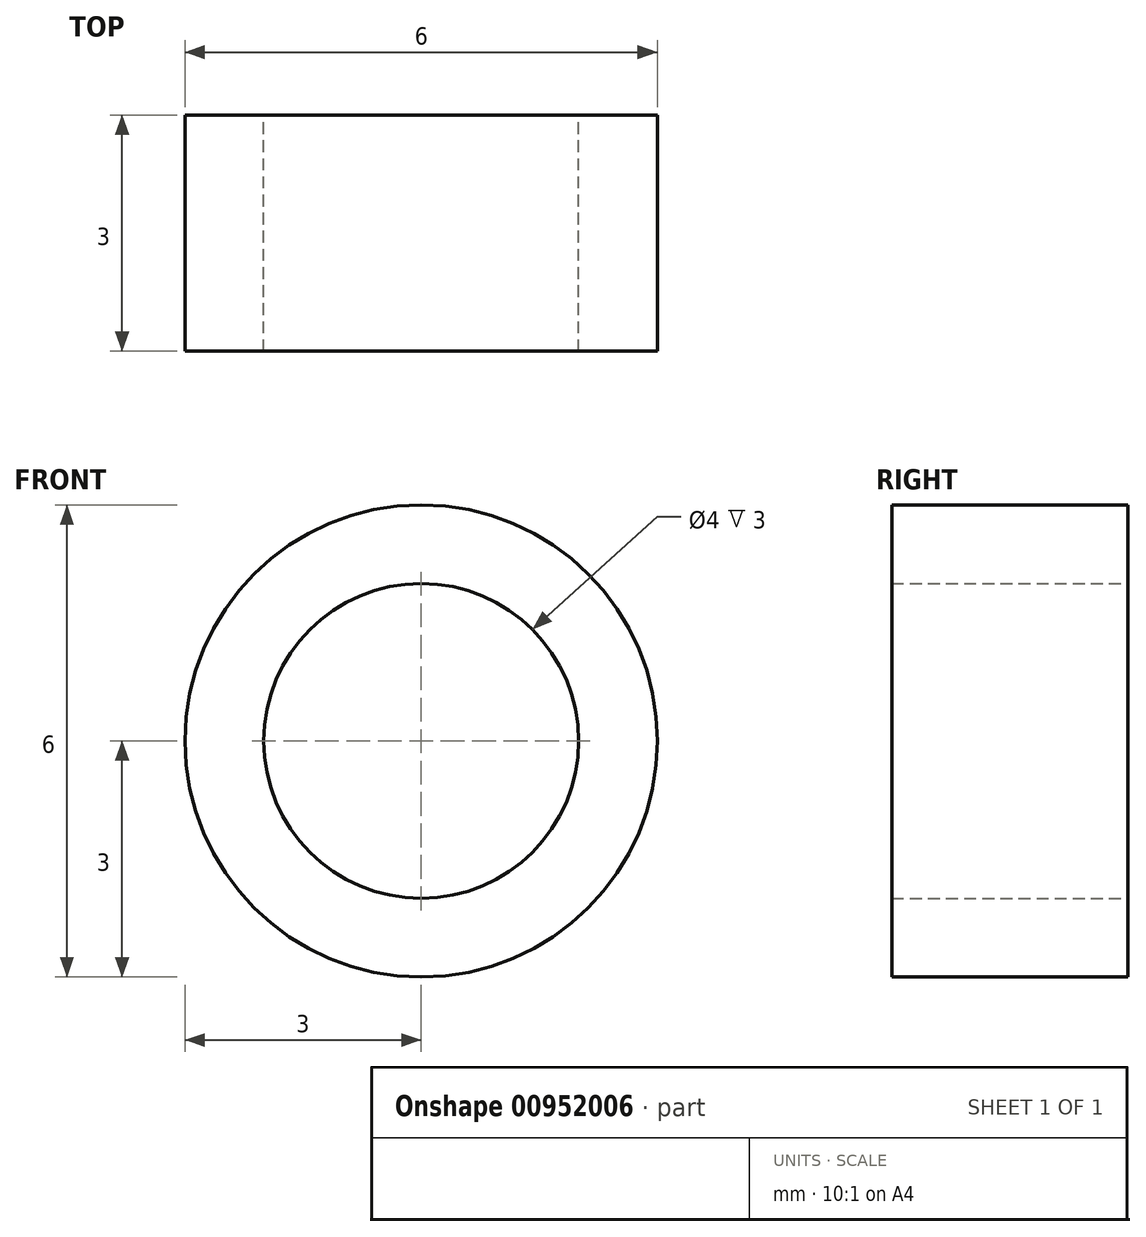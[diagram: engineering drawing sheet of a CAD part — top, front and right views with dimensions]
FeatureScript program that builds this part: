
annotation { "Feature Type Name" : "Feature", "Feature Type Description" : "" }
export const myFeature = defineFeature(function(context is Context, id is Id, definition is map)
    precondition{}
    {
        {
            var Q0;
            Q0=qCreatedBy(makeId("Front.planeOp"),FACE);
            var sketch = newSketch(context, id + "F0", { "sketchPlane" : qUnion([Q0])});
            skCircle(sketch, "E0", {"center": v(0, 0) * mm, "radius": 3 * mm});
            skCircle(sketch, "E1", {"center": v(0, 0) * mm, "radius": 2 * mm});
            skSolve(sketch);
        }
        {
            var Q0;
            Q0 = qSketchRegion(id + "F0", true);
            extrude(context, id + "F1", {"entities" : qUnion([Q0]), "depth" : 3 * mm, "offsetDistance" : 25 * mm});
        }
    });
